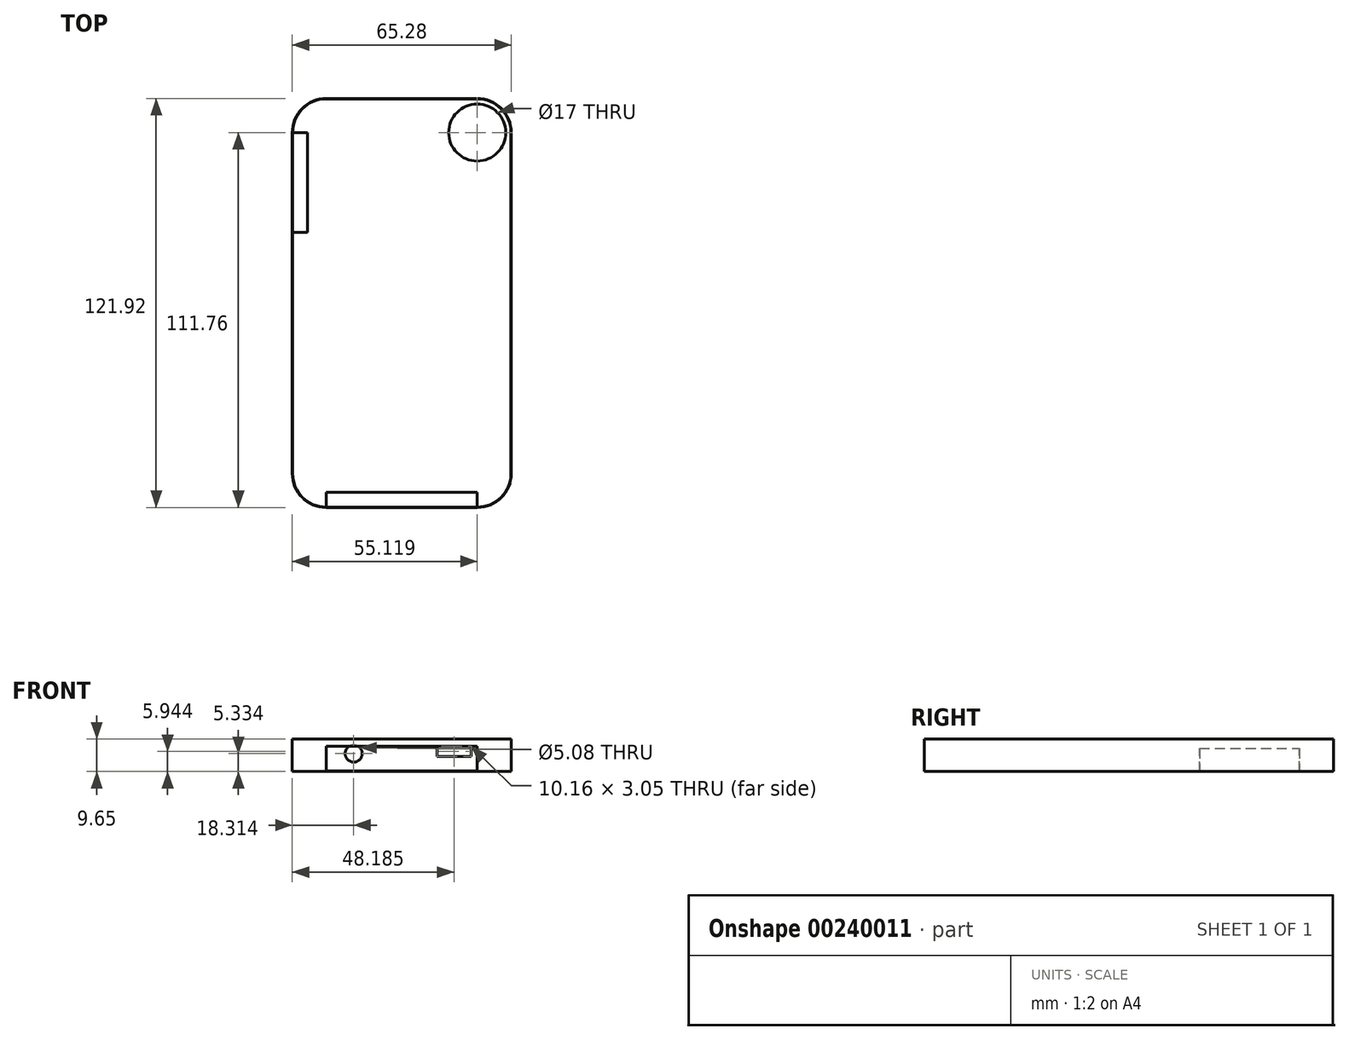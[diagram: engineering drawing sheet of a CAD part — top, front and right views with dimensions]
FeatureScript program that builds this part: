
annotation { "Feature Type Name" : "Feature", "Feature Type Description" : "" }
export const myFeature = defineFeature(function(context is Context, id is Id, definition is map)
    precondition{}
    {
        {
            var Q0;
            Q0=qCreatedBy(makeId("Top.planeOp"),FACE);
            var sketch = newSketch(context, id + "F0", { "sketchPlane" : qUnion([Q0])});
            skLineSegment(sketch, "E0.bottom", {"start": v(-22.48, 60.96) * mm, "end": v(22.48, 60.96) * mm});
            skLineSegment(sketch, "E0.top", {"start": v(-22.48, -60.96) * mm, "end": v(22.48, -60.96) * mm});
            skLineSegment(sketch, "E0.left", {"start": v(-32.64, 50.8) * mm, "end": v(-32.64, -50.8) * mm});
            skLineSegment(sketch, "E0.right", {"start": v(32.64, 50.8) * mm, "end": v(32.64, -50.8) * mm});
            skPoint(sketch, "E0.middle", {"position": v(0, 0) * mm});
            skPoint(sketch, "E1.visualSharp", {"position": v(-32.64, 60.96) * mm});
            skArc(sketch, "E1.filletArc", {"start": v(-22.48, 60.96) * mm, "mid": v(-29.66, 57.98) * mm, "end": v(-32.64, 50.8) * mm});
            skPoint(sketch, "E2.visualSharp", {"position": v(32.64, 60.96) * mm});
            skArc(sketch, "E2.filletArc", {"start": v(32.64, 50.8) * mm, "mid": v(29.66, 57.98) * mm, "end": v(22.48, 60.96) * mm});
            skPoint(sketch, "E3.visualSharp", {"position": v(32.64, -60.96) * mm});
            skArc(sketch, "E3.filletArc", {"start": v(22.48, -60.96) * mm, "mid": v(29.66, -57.98) * mm, "end": v(32.64, -50.8) * mm});
            skPoint(sketch, "E4.visualSharp", {"position": v(-32.64, -60.96) * mm});
            skArc(sketch, "E4.filletArc", {"start": v(-32.64, -50.8) * mm, "mid": v(-29.66, -57.98) * mm, "end": v(-22.48, -60.96) * mm});
            skSolve(sketch);
        }
        {
            var Q0;
            Q0=makeQuery(id+"F0.imprint","IMPRINT",FACE,{"disambiguationData":[TD([[makeQuery(id+"F0.imprint","IMPRINT",EDGE,{"derivedFrom":sQuery(id+"F0.wireOp",EDGE,"E0.bottom")}),-1.0]])]});
            extrude(context, id + "F1", {"entities" : qUnion([Q0]), "depth" : 9.65 * mm});
        }
        {
            var Q0;
            Q0=makeQuery(id+"F1.opExtrude","CAP_FACE",FACE,{"disambiguationData":[OSD([sQuery(id+"F0.wireOp",EDGE,"E0.bottom"),sQuery(id+"F0.wireOp",EDGE,"E0.top"),sQuery(id+"F0.wireOp",EDGE,"E0.left"),sQuery(id+"F0.wireOp",EDGE,"E0.right"),sQuery(id+"F0.wireOp",EDGE,"E1.filletArc"),sQuery(id+"F0.wireOp",EDGE,"E2.filletArc"),sQuery(id+"F0.wireOp",EDGE,"E3.filletArc"),sQuery(id+"F0.wireOp",EDGE,"E4.filletArc")])],"isStart":false});
            shell(context, id + "F2", {"entities" : qUnion([Q0]), "thickness" : 0.13 * mm});
        }
        {
            var Q0;
            Q0=makeQuery(id+"F2.opShell","OFFSET_FACE",FACE,{"disambiguationData":[OSD([sQuery(id+"F0.wireOp",EDGE,"E0.bottom")])]});
            var sketch = newSketch(context, id + "F3", { "sketchPlane" : qUnion([Q0])});
            skLineSegment(sketch, "E5.bottom", {"start": v(20.62, 7.47) * mm, "end": v(10.46, 7.47) * mm});
            skLineSegment(sketch, "E5.top", {"start": v(20.62, 4.42) * mm, "end": v(10.46, 4.42) * mm});
            skLineSegment(sketch, "E5.left", {"start": v(20.62, 7.47) * mm, "end": v(20.62, 4.42) * mm});
            skLineSegment(sketch, "E5.right", {"start": v(10.46, 7.47) * mm, "end": v(10.46, 4.42) * mm});
            skPoint(sketch, "E5.middle", {"position": v(15.54, 5.94) * mm});
            skCircle(sketch, "E6", {"center": v(-14.33, 5.33) * mm, "radius": 2.54 * mm});
            skSolve(sketch);
        }
        {
            var Q0;
            Q0 = qSketchRegion(id + "F3", true);
            extrude(context, id + "F4", {"entities" : qUnion([Q0]), "operationType" : NewBodyOperationType.REMOVE, "oppositeDirection" : true, "depth" : 4.57 * mm});
        }
        {
            var Q0;
            Q0=makeQuery(id+"F1.opExtrude","SWEPT_FACE",FACE,{"disambiguationData":[OSD([sQuery(id+"F0.wireOp",EDGE,"E0.left")])]});
            var sketch = newSketch(context, id + "F5", { "sketchPlane" : qUnion([Q0])});
            skLineSegment(sketch, "E7.bottom", {"start": v(-50.8, 0) * mm, "end": v(-21.03, 0) * mm});
            skLineSegment(sketch, "E7.top", {"start": v(-50.8, 6.86) * mm, "end": v(-21.03, 6.86) * mm});
            skLineSegment(sketch, "E7.left", {"start": v(-50.8, 0) * mm, "end": v(-50.8, 6.86) * mm});
            skLineSegment(sketch, "E7.right", {"start": v(-21.03, 0) * mm, "end": v(-21.03, 6.86) * mm});
            skSolve(sketch);
        }
        {
            var Q0;
            Q0 = qSketchRegion(id + "F5", true);
            extrude(context, id + "F6", {"entities" : qUnion([Q0]), "operationType" : NewBodyOperationType.REMOVE, "oppositeDirection" : true, "depth" : 4.57 * mm});
        }
        {
            var Q0;
            Q0=makeQuery(id+"F1.opExtrude","SWEPT_FACE",FACE,{"disambiguationData":[OSD([sQuery(id+"F0.wireOp",EDGE,"E0.top")])]});
            var sketch = newSketch(context, id + "F7", { "sketchPlane" : qUnion([Q0])});
            skLineSegment(sketch, "E8.bottom", {"start": v(-22.48, 0) * mm, "end": v(22.48, 0) * mm});
            skLineSegment(sketch, "E8.top", {"start": v(-22.48, 7.47) * mm, "end": v(22.48, 7.47) * mm});
            skLineSegment(sketch, "E8.left", {"start": v(-22.48, 0) * mm, "end": v(-22.48, 7.47) * mm});
            skLineSegment(sketch, "E8.right", {"start": v(22.48, 0) * mm, "end": v(22.48, 7.47) * mm});
            skSolve(sketch);
        }
        {
            var Q0;
            Q0 = qSketchRegion(id + "F7", true);
            extrude(context, id + "F8", {"entities" : qUnion([Q0]), "operationType" : NewBodyOperationType.REMOVE, "oppositeDirection" : true, "depth" : 4.57 * mm});
        }
        {
            var Q0;
            Q0=makeQuery(id+"F1.opExtrude","CAP_FACE",FACE,{"disambiguationData":[OSD([sQuery(id+"F0.wireOp",EDGE,"E0.bottom"),sQuery(id+"F0.wireOp",EDGE,"E0.top"),sQuery(id+"F0.wireOp",EDGE,"E0.left"),sQuery(id+"F0.wireOp",EDGE,"E0.right"),sQuery(id+"F0.wireOp",EDGE,"E1.filletArc"),sQuery(id+"F0.wireOp",EDGE,"E2.filletArc"),sQuery(id+"F0.wireOp",EDGE,"E3.filletArc"),sQuery(id+"F0.wireOp",EDGE,"E4.filletArc")])],"isStart":true});
            var sketch = newSketch(context, id + "F9", { "sketchPlane" : qUnion([Q0])});
            skCircle(sketch, "E9", {"center": v(22.48, -50.8) * mm, "radius": 8.5 * mm});
            skSolve(sketch);
        }
        {
            var Q0;
            Q0=makeQuery(id+"F9.imprint","IMPRINT",FACE,{"disambiguationData":[TD([[makeQuery(id+"F9.imprint","IMPRINT",EDGE,{"derivedFrom":sQuery(id+"F9.wireOp",EDGE,"E9")}),1.0]])]});
            extrude(context, id + "F10", {"entities" : qUnion([Q0]), "operationType" : NewBodyOperationType.REMOVE, "oppositeDirection" : true, "depth" : 25.4 * mm});
        }
    });
